# Revit family: Door_Overhead-Sectional_CHI_Full-View
name_source: partatom
category: Doors
units: mm (PartAtom-declared; Revit-internal decimal feet)

## family parameters
Always vertical = Yes
Cut with Voids When Loaded = No
Host = Wall
OmniClass Number = 23.30.10.17.37.14
OmniClass Title = Sectional Overhead Doors
Room Calculation Point = No
Shared = No

## types (1)
- Aluminum
    Analytic Construction = <None>
    Assembly Code = B2030420
    Body Material = Finish - CHI - White Polyester
    Description = CHI Overhead Sectional Door - Aluminum Full View Model 3295
    Expected Lifespan (Years) = 0
    Fire Rating = As Specified in 08360
    Frame Finish = Metal - CHI - Steel
    Function = Exterior
    Glass Type = Glazing - CHI - as Specified
    Is Insulated = Yes
    Keynote = 08360
    Maintenance Schedule (Months) = 0
    Manufacturer = CHI Overhead Doors
    Model = Model 3295
    RO Offset = 0' - 0"
    R_Value = 0
    Revision = R1_02-2013
    Rough Height = 0' - 0"
    Rough Width = 0' - 0"
    Sound Transmission Class (STC) = 0
    Thickness = 0' - 2"
    URL = http://www.chiohd.com
    Wall Closure = By host
    Warranty Duration (Years) = 0

## geometry (parser evidence)
native form markers: Blend x4, Sweep x14
no freeform markers — native parametric forms only
